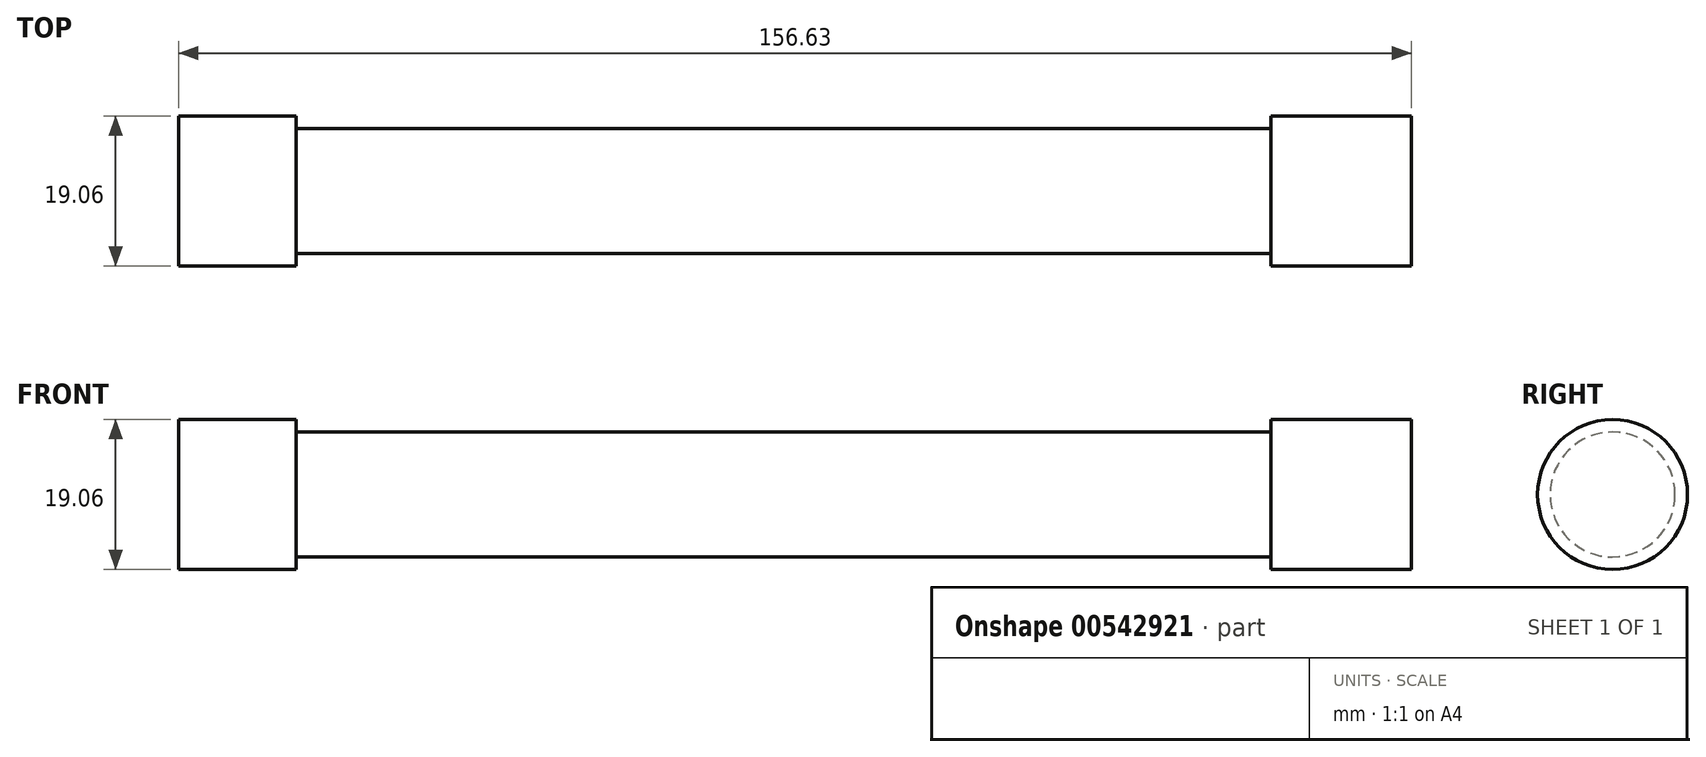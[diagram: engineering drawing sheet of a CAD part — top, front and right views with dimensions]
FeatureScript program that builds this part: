
annotation { "Feature Type Name" : "Feature", "Feature Type Description" : "" }
export const myFeature = defineFeature(function(context is Context, id is Id, definition is map)
    precondition{}
    {
        {
            var Q0;
            Q0=qCreatedBy(makeId("Right.planeOp"),FACE);
            var sketch = newSketch(context, id + "F0", { "sketchPlane" : qUnion([Q0])});
            skCircle(sketch, "E0", {"center": v(0, 0) * mm, "radius": 9.53 * mm});
            skSolve(sketch);
        }
        {
            var Q0;
            Q0=makeQuery(id+"F0.imprint","IMPRINT",FACE,{"disambiguationData":[TD([[makeQuery(id+"F0.imprint","IMPRINT",EDGE,{"derivedFrom":sQuery(id+"F0.wireOp",EDGE,"E0")}),1.0]])]});
            extrude(context, id + "F1", {"entities" : qUnion([Q0]), "depth" : 6.35 * mm, "offsetDistance" : 25.4 * mm, "hasSecondDirection" : true, "secondDirectionOppositeDirection" : true, "secondDirectionDepth" : 8.6 * mm});
        }
        {
            var Q0;
            Q0=makeQuery(id+"F1.opExtrude","CAP_FACE",FACE,{"disambiguationData":[OSD([sQuery(id+"F0.wireOp",EDGE,"E0")])],"isStart":false});
            var sketch = newSketch(context, id + "F2", { "sketchPlane" : qUnion([Q0])});
            skCircle(sketch, "E1", {"center": v(0, 0) * mm, "radius": 7.94 * mm});
            skSolve(sketch);
        }
        {
            var Q0;
            Q0=makeQuery(id+"F2.imprint","IMPRINT",FACE,{"disambiguationData":[TD([[makeQuery(id+"F2.imprint","IMPRINT",EDGE,{"derivedFrom":sQuery(id+"F2.wireOp",EDGE,"E1")}),1.0]])]});
            extrude(context, id + "F3", {"entities" : qUnion([Q0]), "operationType" : NewBodyOperationType.ADD, "depth" : 123.82 * mm, "offsetDistance" : 25.4 * mm});
        }
        {
            var Q0;
            Q0=makeQuery(id+"F3.opExtrude","CAP_FACE",FACE,{"disambiguationData":[OSD([sQuery(id+"F2.wireOp",EDGE,"E1")])],"isStart":false});
            var sketch = newSketch(context, id + "F4", { "sketchPlane" : qUnion([Q0])});
            skCircle(sketch, "E2", {"center": v(0, 0) * mm, "radius": 9.53 * mm});
            skSolve(sketch);
        }
        {
            var Q0;
            Q0 = qSketchRegion(id + "F4", true);
            extrude(context, id + "F5", {"entities" : qUnion([Q0]), "depth" : 15.24 * mm, "offsetDistance" : 25.4 * mm});
        }
        {
            var Q0;
            Q0=makeQuery(id+"F5.opExtrude","CAP_FACE",FACE,{"disambiguationData":[OSD([sQuery(id+"F4.wireOp",EDGE,"E2")])],"isStart":false});
            extrude(context, id + "F6", {"entities" : qUnion([Q0]), "operationType" : NewBodyOperationType.ADD, "depth" : 2.62 * mm, "offsetDistance" : 25.4 * mm});
        }
    });
